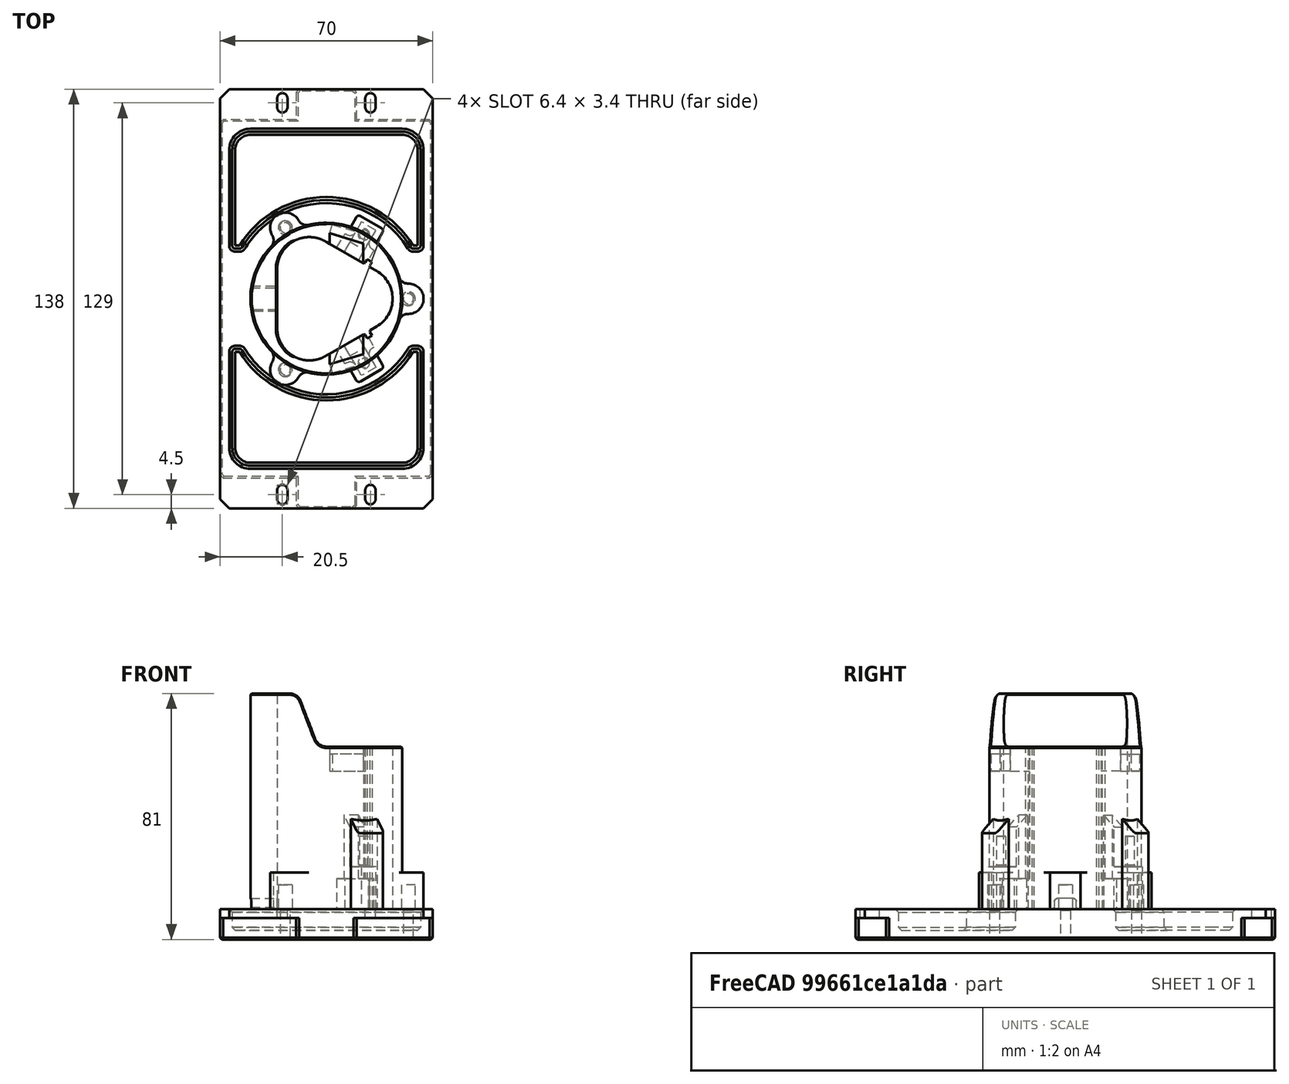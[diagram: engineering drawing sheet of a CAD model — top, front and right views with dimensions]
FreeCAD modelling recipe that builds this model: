
FCSTD DOCUMENT  (FreeCAD 1.2R20260204 (Git shallow))
Label: SupportBatterie
License: All rights reserved
LicenseURL: https://en.wikipedia.org/wiki/All_rights_reserved
objects: Sketcher::SketchObject×17, PartDesign::Pocket×12, PartDesign::Chamfer×11, PartDesign::Fillet×8, PartDesign::Pad×6, PartDesign::Mirrored×4, Image::ImagePlane×3, App::Point×3, PartDesign::Draft×2, PartDesign::Body×2, App::DocumentObjectGroup×1, PartDesign::PolarPattern×1, PartDesign::SubShapeBinder×1, App::Part×1
note: 164 computed .brp shape members not serialized (recipe doc carries the construction recipe); baked Part::Feature solids carry a one-line shape summary decoded from their .brp

FEATURE [Image::ImagePlane] IMG_20250729_205622
  Placement = pos=(4.02698,3.13465,0.3) rot=(0,0,1;0.021991rad)
  XSize = 54.8631
  YSize = 121.865
FEATURE [Image::ImagePlane] IMG_20250729_205825
  Placement = pos=(5.3,0,28.7) rot=(0.57735,0.57735,-0.57735;2.0944rad)
  XSize = 200.469
  YSize = 90.2503
FEATURE [Sketcher::SketchObject] Sketch
  ArcFitTolerance = 1e-06
  AttachmentSupport = -> [XY_Plane]
  ExternalTypes = [0]
  FullyConstrained = true
  MakeInternals = false
  MapMode = 5
  sketch-geometry (21):
    g0: ArcOfCircle CenterX=11.2267 CenterY=0 CenterZ=0 NormalX=0 NormalY=0 NormalZ=1 AngleXU=0 Radius=10.58 StartAngle=5.23599 EndAngle=7.33038
    g1: ArcOfCircle CenterX=-5.61333 CenterY=9.72258 CenterZ=0 NormalX=0 NormalY=0 NormalZ=1 AngleXU=0 Radius=10.58 StartAngle=1.0472 EndAngle=3.14159
    g2: ArcOfCircle CenterX=-5.61333 CenterY=-9.72258 CenterZ=0 NormalX=0 NormalY=0 NormalZ=1 AngleXU=0 Radius=10.58 StartAngle=3.14159 EndAngle=5.23599
    g3: LineSegment [constr] StartX=-0.323333 StartY=18.8851 StartZ=0 EndX=16.5167 EndY=9.16255 EndZ=0
    g4: LineSegment [constr] StartX=16.5167 StartY=-9.16255 StartZ=0 EndX=-0.323333 EndY=-18.8851 EndZ=0
    g5: LineSegment StartX=-16.1933 StartY=-9.72258 StartZ=0 EndX=-16.1933 EndY=9.72258 EndZ=0
    g6: LineSegment [constr] StartX=-5.61333 StartY=9.72258 StartZ=0 EndX=9e-16 EndY=0 EndZ=0
    g7: LineSegment [constr] StartX=0 StartY=0 StartZ=0 EndX=11.2267 EndY=0 EndZ=0
    g8: LineSegment [constr] StartX=0 StartY=0 StartZ=0 EndX=-5.61333 EndY=-9.72258 EndZ=0
    g9: GeomPoint [constr] X=21.8067 Y=0 Z=0
    g10: Circle CenterX=0 CenterY=0 CenterZ=0 NormalX=0 NormalY=0 NormalZ=1 AngleXU=0 Radius=25
    g11: LineSegment StartX=12.55 StartY=11.4527 StartZ=0 EndX=13.45 EndY=13.0116 EndZ=0
    g12: LineSegment StartX=13.45 StartY=13.0116 StartZ=0 EndX=15.0088 EndY=12.1116 EndZ=0
    g13: LineSegment StartX=15.0088 StartY=12.1116 StartZ=0 EndX=14.1088 EndY=10.5527 EndZ=0
    g14: LineSegment StartX=12.55 StartY=-11.4527 StartZ=0 EndX=13.45 EndY=-13.0116 EndZ=0
    g15: LineSegment StartX=13.45 StartY=-13.0116 StartZ=0 EndX=15.0088 EndY=-12.1116 EndZ=0
    g16: LineSegment StartX=15.0088 StartY=-12.1116 StartZ=0 EndX=14.1088 EndY=-10.5527 EndZ=0
    g17: LineSegment StartX=-0.323333 StartY=18.8851 StartZ=0 EndX=12.55 EndY=11.4527 EndZ=0
    g18: LineSegment StartX=14.1088 StartY=10.5527 StartZ=0 EndX=16.5167 EndY=9.16255 EndZ=0
    g19: LineSegment StartX=14.1088 StartY=-10.5527 StartZ=0 EndX=16.5167 EndY=-9.16255 EndZ=0
    g20: LineSegment StartX=12.55 StartY=-11.4527 StartZ=0 EndX=-0.323333 EndY=-18.8851 EndZ=0
  constraints (52):
    c: Equal(g1,g2)
    c: Equal(g2,g0)
    c: Vertical(g5)
    c: Tangent(g5,g1) = 1.5708
    c: Tangent(g3,g1) = 1.5708
    c: Tangent(g3,g0) = 1.5708
    c: Tangent(g4,g0) = 1.5708
    c: Tangent(g4,g2) = 1.5708
    c: Tangent(g5,g2) = 1.5708
    c: PointOnObject(g0,g-1)
    c: Equal(g5,g4)
    c: Equal(g4,g3)
    c: Coincident(g6,g1)
    c: Coincident(g6,g-1)
    c: Coincident(g7,g6)
    c: Coincident(g7,g0)
    c: Coincident(g8,g6)
    c: Coincident(g8,g2)
    c: Equal(g6,g7)
    c: PointOnObject(g9,g-1)
    c: PointOnObject(g9,g0)
    c: DistanceX(g1,g9) = 38
    c: Radius(g0) = 10.58
    c: Coincident(g10,g6)
    c: Diameter(g10) = 50
    c: PointOnObject(g11,g3)
    c: Coincident(g11,g12)
    c: Coincident(g12,g13)
    c: PointOnObject(g13,g3)
    c: Perpendicular(g12,g11)
    c: Perpendicular(g13,g12)
    c: Perpendicular(g3,g11)
    c: PointOnObject(g14,g4)
    c: Coincident(g14,g15)
    c: Coincident(g15,g16)
    c: Perpendicular(g15,g16)
    c: Perpendicular(g14,g15)
    c: Perpendicular(g4,g16)
    c: Equal(g15,g12)
    c: Symmetric(g13,g16,g-1)
    c: Equal(g13,g16)
    c: Distance(g12) = 1.8
    c: Distance(g11) = 1.8
    c: DistanceX(g10,g11) = 12.55
    c: Coincident(g17,g1)
    c: Coincident(g17,g11)
    c: Coincident(g18,g13)
    c: Coincident(g18,g0)
    c: Coincident(g19,g16)
    c: Coincident(g19,g0)
    c: Coincident(g20,g14)
    c: Coincident(g20,g2)
FEATURE [PartDesign::Pad] Pad
  AlongSketchNormal = false
  Direction = (0,0,1)
  Length = 61
  Length2 = 10
  Profile = -> Sketch
  ReferenceAxis = -> Sketch [N_Axis]
  Refine = true
  SideType = 0
  Suppressed = false
  Type = 0
  Type2 = 0
FEATURE [Sketcher::SketchObject] Sketch001
  ArcFitTolerance = 1e-06
  AttachmentSupport = -> [XY_Plane]
  ExternalGeometry = -> [Pad]
  ExternalTypes = [0]
  FullyConstrained = true
  MakeInternals = false
  MapMode = 5
  sketch-geometry (8):
    g0: LineSegment StartX=4.91 StartY=15.8637 StartZ=0 EndX=3.455 EndY=13.3435 EndZ=0
    g1: LineSegment StartX=3.455 StartY=13.3435 StartZ=0 EndX=9.99349 EndY=9.56853 EndZ=0
    g2: LineSegment StartX=9.99349 StartY=9.56853 StartZ=0 EndX=11.4485 EndY=12.0887 EndZ=0
    g3: LineSegment StartX=11.4485 StartY=12.0887 StartZ=0 EndX=4.91 EndY=15.8637 EndZ=0
    g4: LineSegment StartX=4.91 StartY=-15.8637 StartZ=0 EndX=3.455 EndY=-13.3435 EndZ=0
    g5: LineSegment StartX=3.455 StartY=-13.3435 StartZ=0 EndX=9.99349 EndY=-9.56853 EndZ=0
    g6: LineSegment StartX=9.99349 StartY=-9.56853 StartZ=0 EndX=11.4485 EndY=-12.0887 EndZ=0
    g7: LineSegment StartX=11.4485 StartY=-12.0887 StartZ=0 EndX=4.91 EndY=-15.8637 EndZ=0
  constraints (23):
    c: PointOnObject(g0,g-3)
    c: Coincident(g0,g1)
    c: Coincident(g1,g2)
    c: PointOnObject(g2,g-3)
    c: Coincident(g2,g3)
    c: Coincident(g3,g0)
    c: PointOnObject(g4,g-4)
    c: Coincident(g4,g5)
    c: Coincident(g5,g6)
    c: Coincident(g6,g7)
    c: Coincident(g7,g4)
    c: Equal(g7,g5)
    c: Equal(g5,g1)
    c: Equal(g1,g3)
    c: Equal(g2,g0)
    c: Equal(g0,g6)
    c: Equal(g6,g4)
    c: Perpendicular(g2,g1)
    c: Perpendicular(g6,g7)
    c: Symmetric(g6,g2,g-1)
    c: Distance(g3) = 7.55
    c: Distance(g2) = 2.91
    c: DistanceX(g-1,g0) = 4.91
FEATURE [PartDesign::Pad] Pad001
  AlongSketchNormal = false
  BaseFeature = -> Pad
  Direction = (0,0,1)
  Length = 1.5
  Length2 = 10
  Profile = -> Sketch001
  ReferenceAxis = -> Sketch001 [N_Axis]
  Refine = true
  SideType = 0
  Suppressed = false
  Type = 0
  Type2 = 0
FEATURE [PartDesign::Chamfer] Chamfer
  Angle = 45
  Base = -> Pad001 [Edge29,Edge35,Edge23,Edge18]
  BaseFeature = -> Pad001
  ChamferType = 0
  FlipDirection = false
  Refine = true
  Size = 0.4
  Size2 = 1
  SupportTransform = false
  Suppressed = false
  UseAllEdges = false
FEATURE [PartDesign::Fillet] Fillet
  Base = -> Chamfer [Edge81,Edge77,Edge72,Edge76]
  BaseFeature = -> Chamfer
  Radius = 0.6
  Refine = true
  SupportTransform = false
  Suppressed = false
  UseAllEdges = false
FEATURE [PartDesign::Chamfer] Chamfer001
  Angle = 45
  Base = -> Fillet [Face32]
  BaseFeature = -> Fillet
  ChamferType = 0
  FlipDirection = false
  Refine = true
  Size = 0.4
  Size2 = 1
  SupportTransform = false
  Suppressed = false
  UseAllEdges = false
FEATURE [Sketcher::SketchObject] Sketch002
  ArcFitTolerance = 1e-06
  AttachmentSupport = -> [XZ_Plane]
  ExternalGeometry = -> [Chamfer001]
  ExternalTypes = [0]
  FullyConstrained = true
  MakeInternals = false
  MapMode = 5
  Placement = pos=(0,0,0) rot=(1,0,0;1.5708rad)
  sketch-geometry (4):
    g0: LineSegment StartX=-9.41 StartY=61 StartZ=0 EndX=-2.71 EndY=43.5 EndZ=0
    g1: LineSegment StartX=-2.71 StartY=43.5 StartZ=0 EndX=25 EndY=43.5 EndZ=0
    g2: LineSegment StartX=25 StartY=43.5 StartZ=0 EndX=25 EndY=61 EndZ=0
    g3: LineSegment StartX=-9.41 StartY=61 StartZ=0 EndX=25 EndY=61 EndZ=0
  constraints (12):
    c: Coincident(g1,g0)
    c: Coincident(g2,g1)
    c: Vertical(g2)
    c: Coincident(g3,g0)
    c: Coincident(g3,g2)
    c: Horizontal(g3)
    c: Horizontal(g1)
    c: DistanceY(g2,g2) = 17.5
    c: PointOnObject(g-3,g3)
    c: PointOnObject(g-4,g2)
    c: DistanceX(g3,g3) = 34.41
    c: DistanceX(g1,g1) = 27.71
FEATURE [PartDesign::Pocket] Pocket
  AlongSketchNormal = false
  BaseFeature = -> Chamfer001
  Direction = (0,1,-2e-16)
  Length = 60
  Length2 = 10
  Profile = -> Sketch002
  ReferenceAxis = -> Sketch002 [N_Axis]
  Refine = true
  SideType = 2
  Suppressed = false
  Type = 0
  Type2 = 0
FEATURE [PartDesign::Fillet] Fillet001
  Base = -> Pocket [Edge106,Edge67,Edge51,Edge111]
  BaseFeature = -> Pocket
  Radius = 4
  Refine = true
  SupportTransform = false
  Suppressed = false
  UseAllEdges = false
FEATURE [Image::ImagePlane] IMG_20250729_205826  label="IMG_20250729_205826_205826"
  Placement = pos=(4.02698,3.13465,43.6) rot=(0,0,1;0.021991rad)
  XSize = 54.8631
  YSize = 121.865
FEATURE [Sketcher::SketchObject] Sketch003
  ArcFitTolerance = 1e-06
  AttachmentSupport = -> [Fillet001]
  ExternalGeometry = -> [Fillet001]
  ExternalTypes = [0]
  FullyConstrained = true
  MakeInternals = false
  MapMode = 5
  Placement = pos=(0,9.7e-15,43.5) rot=(0,0,1;0rad)
  sketch-geometry (4):
    g0: LineSegment StartX=1.07 StartY=18.0807 StartZ=0 EndX=1.07 EndY=21.5807 EndZ=0
    g1: LineSegment StartX=12.07 StartY=18.2298 StartZ=0 EndX=12.07 EndY=11.7298 EndZ=0
    g2: LineSegment StartX=1.07 StartY=18.0807 StartZ=0 EndX=12.07 EndY=11.7298 EndZ=0
    g3: LineSegment StartX=1.07 StartY=21.5807 StartZ=0 EndX=12.07 EndY=18.2298 EndZ=0
  constraints (12):
    c: Vertical(g0)
    c: Vertical(g1)
    c: Coincident(g2,g0)
    c: Coincident(g2,g1)
    c: DistanceX(g0) = 1.07
    c: DistanceY(g0,g0) = 3.5
    c: DistanceY(g1,g1) = 6.5
    c: DistanceX(g0,g1) = 11
    c: Coincident(g3,g0)
    c: Coincident(g3,g1)
    c: PointOnObject(g0,g-3)
    c: PointOnObject(g1,g-3)
FEATURE [PartDesign::Pocket] Pocket001
  AlongSketchNormal = false
  BaseFeature = -> Fillet001
  Direction = (0,0,-1)
  Length = 8
  Length2 = 10
  Profile = -> Sketch003
  ReferenceAxis = -> Sketch003 [N_Axis]
  Refine = true
  SideType = 0
  Suppressed = false
  Type = 0
  Type2 = 0
FEATURE [Sketcher::SketchObject] Sketch004
  ArcFitTolerance = 1e-06
  AttachmentSupport = -> [Pocket001]
  ExternalGeometry = -> [Pocket001]
  ExternalTypes = [0]
  FullyConstrained = true
  MakeInternals = false
  MapMode = 5
  Placement = pos=(6.1066,20.0464,0) rot=(0.978531,-0.145736,-0.145736;1.5925rad)
  sketch-geometry (4):
    g0: LineSegment StartX=-5.2651 StartY=35.5 StartZ=0 EndX=6.23395 EndY=35.5 EndZ=0
    g1: LineSegment StartX=6.23395 StartY=35.5 StartZ=0 EndX=6.23395 EndY=41 EndZ=0
    g2: LineSegment StartX=6.23395 StartY=41 StartZ=0 EndX=-5.2651 EndY=41 EndZ=0
    g3: LineSegment StartX=-5.2651 StartY=41 StartZ=0 EndX=-5.2651 EndY=35.5 EndZ=0
  constraints (11):
    c: Coincident(g0,g1)
    c: Coincident(g1,g2)
    c: Coincident(g2,g3)
    c: Coincident(g3,g0)
    c: Horizontal(g2)
    c: Vertical(g1)
    c: Vertical(g3)
    c: Coincident(g0,g-3)
    c: Coincident(g0,g-3)
    c: DistanceY(g1,g1) = 5.5
    c: DistanceY(g1,g-4) = 2.5
FEATURE [PartDesign::Pocket] Pocket002
  AlongSketchNormal = false
  BaseFeature = -> Pocket001
  Direction = (0.291403,0.956601,1e-16)
  Length = 3
  Length2 = 10
  Profile = -> Sketch004
  ReferenceAxis = -> Sketch004 [N_Axis]
  Refine = true
  SideType = 0
  Suppressed = false
  Type = 0
  Type2 = 0
FEATURE [PartDesign::Mirrored] Mirrored
  BaseFeature = -> Pocket002
  MirrorPlane = -> XZ_Plane
  Originals = -> [Pocket001,Pocket002]
  Refine = true
  Suppressed = false
  TransformMode = 0
FEATURE [PartDesign::Chamfer] Chamfer002
  Angle = 45
  Base = -> Mirrored [Edge19]
  BaseFeature = -> Mirrored
  ChamferType = 0
  FlipDirection = false
  Refine = true
  Size = 0.4
  Size2 = 1
  SupportTransform = false
  Suppressed = false
  UseAllEdges = false
FEATURE [App::DocumentObjectGroup] Group  label="Images"
  Group = -> [IMG_20250729_205622,IMG_20250729_205825,IMG_20250729_205826]
FEATURE [App::Point] Origin001  label="Origine"
  Role = Origin
FEATURE [Sketcher::SketchObject] Sketch005
  ArcFitTolerance = 1e-06
  AttachmentSupport = -> [Chamfer002]
  ExternalGeometry = -> [Chamfer002]
  ExternalTypes = [0,0,0]
  FullyConstrained = true
  MakeInternals = false
  MapMode = 5
  Placement = pos=(0,0,0) rot=(1,0,0;3.14159rad)
  sketch-geometry (13):
    g0: LineSegment [constr] StartX=4.91 StartY=15.8637 StartZ=0 EndX=11.4485 EndY=12.0887 EndZ=0
    g1: LineSegment [constr] StartX=7.79768 StartY=18.8153 StartZ=0 EndX=4.34268 EndY=12.831 EndZ=0
    g2: LineSegment [constr] StartX=4.34268 StartY=12.831 StartZ=0 EndX=9.10582 EndY=10.081 EndZ=0
    g3: LineSegment [constr] StartX=9.10582 StartY=10.081 StartZ=0 EndX=12.5608 EndY=16.0653 EndZ=0
    g4: LineSegment StartX=12.5608 StartY=16.0653 StartZ=0 EndX=7.79768 EndY=18.8153 EndZ=0
    g5: GeomPoint X=6.72425 Y=11.456 Z=0
    g6: LineSegment StartX=7.79768 StartY=18.8153 StartZ=0 EndX=5.79768 EndY=15.3512 EndZ=0
    g7: LineSegment StartX=4.91 StartY=15.8637 StartZ=0 EndX=3.45499 EndY=13.3435 EndZ=0
    g8: LineSegment StartX=3.45499 StartY=13.3435 StartZ=0 EndX=9.99349 EndY=9.56853 EndZ=0
    g9: LineSegment StartX=9.99349 StartY=9.56853 StartZ=0 EndX=11.4485 EndY=12.0887 EndZ=0
    g10: LineSegment StartX=11.4485 StartY=12.0887 StartZ=0 EndX=10.5608 EndY=12.6012 EndZ=0
    g11: LineSegment StartX=10.5608 StartY=12.6012 StartZ=0 EndX=12.5608 EndY=16.0653 EndZ=0
    g12: LineSegment StartX=4.91 StartY=15.8637 StartZ=0 EndX=5.79768 EndY=15.3512 EndZ=0
  constraints (32):
    c: Coincident(g0,g-3)
    c: Coincident(g0,g-4)
    c: Coincident(g1,g2)
    c: Coincident(g2,g3)
    c: Coincident(g3,g4)
    c: Coincident(g4,g1)
    c: Parallel(g1,g3)
    c: Parallel(g2,g4)
    c: Perpendicular(g1,g2)
    c: PointOnObject(g1,g-5)
    c: Distance(g0,g4) = 4
    c: Symmetric(g2,g2,g5)
    c: Symmetric(g-5,g-5,g5)
    c: Coincident(g6,g1)
    c: PointOnObject(g6,g1)
    c: Coincident(g7,g0)
    c: Coincident(g8,g7)
    c: Coincident(g9,g8)
    c: Coincident(g9,g0)
    c: Coincident(g10,g0)
    c: PointOnObject(g10,g3)
    c: Coincident(g11,g10)
    c: Coincident(g11,g3)
    c: Distance(g4,g4) = 5.5
    c: PointOnObject(g10,g0)
    c: PointOnObject(g6,g0)
    c: Coincident(g12,g0)
    c: Coincident(g12,g6)
    c: PointOnObject(g-5,g8)
    c: PointOnObject(g-5,g8)
    c: Equal(g7,g9)
    c: Perpendicular(g10,g9)
FEATURE [PartDesign::Pocket] Pocket003
  BaseFeature = -> Chamfer002
  Direction = (0,0,1)
  Length = 17
  Length2 = 5
  Profile = -> Sketch005
  ReferenceAxis = -> Sketch005 [N_Axis]
  Refine = true
  SideType = 0
  Suppressed = false
  Type = 0
  Type2 = 0
FEATURE [PartDesign::Draft] Draft
  Angle = -45
  Base = -> Pocket003 [Face55]
  BaseFeature = -> Pocket003
  NeutralPlane = -> Pocket003 [Face56]
  Refine = true
  SupportTransform = false
  Suppressed = false
FEATURE [Sketcher::SketchObject] Sketch006
  ArcFitTolerance = 1e-06
  AttachmentSupport = -> [Draft]
  ExternalGeometry = -> [Draft]
  ExternalTypes = [0]
  FullyConstrained = true
  MakeInternals = false
  MapMode = 5
  Placement = pos=(0,0,0) rot=(1,0,0;3.14159rad)
  sketch-geometry (5):
    g0: LineSegment StartX=5.84912 StartY=19.9403 StartZ=0 EndX=14.5094 EndY=14.9403 EndZ=0
    g1: LineSegment StartX=14.5094 StartY=14.9403 StartZ=0 EndX=19.0094 EndY=22.7345 EndZ=0
    g2: LineSegment StartX=19.0094 StartY=22.7345 StartZ=0 EndX=10.3491 EndY=27.7345 EndZ=0
    g3: LineSegment StartX=10.3491 StartY=27.7345 StartZ=0 EndX=5.84912 EndY=19.9403 EndZ=0
    g4: GeomPoint X=10.1792 Y=17.4403 Z=0
  constraints (12):
    c: Coincident(g0,g1)
    c: Coincident(g1,g2)
    c: Coincident(g2,g3)
    c: Coincident(g3,g0)
    c: Parallel(g0,g2)
    c: Parallel(g1,g3)
    c: PointOnObject(g0,g-3)
    c: Perpendicular(g1,g0)
    c: Symmetric(g0,g0,g4)
    c: Symmetric(g-3,g-3,g4)
    c: Distance(g2,g2) = 10
    c: Distance(g1,g1) = 9
FEATURE [PartDesign::Pad] Pad002
  BaseFeature = -> Draft
  Direction = (0,0,-1)
  Length = 15
  Length2 = 10
  Profile = -> Sketch006
  ReferenceAxis = -> Sketch006 [N_Axis]
  Refine = true
  Reversed = true
  SideType = 0
  Suppressed = false
  Type = 0
  Type2 = 0
FEATURE [PartDesign::Draft] Draft001
  Angle = 45
  Base = -> Pad002 [Face57]
  BaseFeature = -> Pad002
  NeutralPlane = -> Pad002 [Face68]
  Refine = true
  SupportTransform = false
  Suppressed = false
FEATURE [PartDesign::Fillet] Fillet002
  Base = -> Draft001 [Edge178,Edge182]
  BaseFeature = -> Draft001
  Radius = 1
  Refine = true
  SupportTransform = false
  Suppressed = false
  UseAllEdges = false
FEATURE [Sketcher::SketchObject] Sketch007
  ArcFitTolerance = 1e-06
  AttachmentSupport = -> [Fillet002]
  ExternalGeometry = -> [Fillet002]
  ExternalTypes = [0]
  FullyConstrained = true
  MakeInternals = false
  MapMode = 5
  Placement = pos=(0,0,0) rot=(1,0,0;3.14159rad)
  sketch-geometry (4):
    g0: LineSegment StartX=7.79768 StartY=18.8153 StartZ=0 EndX=12.5608 EndY=16.0653 EndZ=0
    g1: LineSegment StartX=12.5608 StartY=16.0653 StartZ=0 EndX=16.3108 EndY=22.5605 EndZ=0
    g2: LineSegment StartX=16.3108 StartY=22.5605 StartZ=0 EndX=11.5477 EndY=25.3105 EndZ=0
    g3: LineSegment StartX=11.5477 StartY=25.3105 StartZ=0 EndX=7.79768 EndY=18.8153 EndZ=0
  constraints (10):
    c: Coincident(g0,g1)
    c: Coincident(g1,g2)
    c: Coincident(g2,g3)
    c: Coincident(g3,g0)
    c: Parallel(g0,g2)
    c: Parallel(g1,g3)
    c: Perpendicular(g1,g0)
    c: Coincident(g0,g-3)
    c: Coincident(g0,g-3)
    c: Distance(g1,g1) = 7.5
FEATURE [PartDesign::Pocket] Pocket004
  BaseFeature = -> Fillet002
  Direction = (0,0,1)
  Length = 4
  Length2 = 5
  Profile = -> Sketch007
  ReferenceAxis = -> Sketch007 [N_Axis]
  Refine = true
  SideType = 0
  Suppressed = false
  Type = 0
  Type2 = 0
FEATURE [Sketcher::SketchObject] Sketch008
  ArcFitTolerance = 1e-06
  AttachmentSupport = -> [Pocket004]
  ExternalGeometry = -> [Pocket004]
  ExternalTypes = [0]
  FullyConstrained = true
  MakeInternals = false
  MapMode = 5
  Placement = pos=(0,0,4) rot=(1,0,0;3.14159rad)
  sketch-geometry (2):
    g0: Circle CenterX=12.3292 CenterY=21.1642 CenterZ=0 NormalX=0 NormalY=0 NormalZ=1 AngleXU=0 Radius=1.5
    g1: LineSegment [constr] StartX=10.1792 StartY=17.4403 StartZ=0 EndX=13.9292 EndY=23.9355 EndZ=0
  constraints (5):
    c: Diameter(g0) = 3
    c: Symmetric(g-3,g-3,g1)
    c: Symmetric(g-5,g-5,g1)
    c: PointOnObject(g0,g1)
    c: Distance(g0,g-3) = 4.3
FEATURE [PartDesign::Pocket] Pocket005
  BaseFeature = -> Pocket004
  Direction = (0,0,1)
  Length = 10
  Length2 = 5
  Profile = -> Sketch008
  ReferenceAxis = -> Sketch008 [N_Axis]
  Refine = true
  SideType = 0
  Suppressed = false
  Type = 0
  Type2 = 0
FEATURE [PartDesign::Chamfer] Chamfer003
  Angle = 45
  Base = -> Pocket005 [Edge156]
  BaseFeature = -> Pocket005
  ChamferType = 0
  FlipDirection = false
  Refine = true
  Size = 0.4
  Size2 = 1
  SupportTransform = false
  Suppressed = false
  UseAllEdges = false
FEATURE [PartDesign::Mirrored] Mirrored001
  BaseFeature = -> Chamfer003
  MirrorPlane = -> XZ_Plane
  Originals = -> [Pocket003,Draft,Pad002,Draft001,Fillet002,Pocket004,Pocket005,Chamfer003]
  Refine = true
  Suppressed = false
  TransformMode = 0
FEATURE [PartDesign::Pad] Pad003
  BaseFeature = -> Mirrored001
  Direction = (0,0,-1)
  Length = 10
  Length2 = 10
  Profile = -> Mirrored001 [Face76]
  Refine = true
  SideType = 0
  Suppressed = false
  Type = 0
  Type2 = 0
FEATURE [Sketcher::SketchObject] Sketch009
  ArcFitTolerance = 1e-06
  AttachmentSupport = -> [Pad003]
  ExternalGeometry = -> [Pad003]
  ExternalTypes = [0,0,0,0,0,0]
  FullyConstrained = true
  MakeInternals = false
  MapMode = 5
  Placement = pos=(0,0,-10) rot=(1,0,0;3.14159rad)
  sketch-geometry (7):
    g0: ArcOfCircle [constr] CenterX=0 CenterY=0 CenterZ=0 NormalX=0 NormalY=0 NormalZ=1 AngleXU=0 Radius=5 StartAngle=1.5708 EndAngle=4.71239
    g1: ArcOfCircle CenterX=27 CenterY=0 CenterZ=0 NormalX=0 NormalY=0 NormalZ=1 AngleXU=0 Radius=5 StartAngle=4.71239 EndAngle=7.85398
    g2: LineSegment [constr] StartX=-8e-16 StartY=5 StartZ=0 EndX=27 EndY=5 EndZ=0
    g3: LineSegment [constr] StartX=-9e-16 StartY=-5 StartZ=0 EndX=27 EndY=-5 EndZ=0
    g4: ArcOfCircle CenterX=0 CenterY=0 CenterZ=0 NormalX=0 NormalY=0 NormalZ=1 AngleXU=0 Radius=25 StartAngle=6.08183 EndAngle=6.48454
    g5: LineSegment StartX=24.4949 StartY=5 StartZ=0 EndX=27 EndY=5 EndZ=0
    g6: LineSegment StartX=27 StartY=-5 StartZ=0 EndX=24.4949 EndY=-5 EndZ=0
  constraints (17):
    c: Tangent(g0,g2) = 1.5708
    c: Tangent(g0,g3) = -1.5708
    c: Tangent(g1,g2) = 1.5708
    c: Tangent(g1,g3) = -1.5708
    c: Equal(g0,g1)
    c: Coincident(g0,g-5)
    c: DistanceX(g-5,g1) = 2
    c: Distance(g1,g1) = 10
    c: PointOnObject(g1,g-1)
    c: Coincident(g4,g0)
    c: PointOnObject(g4,g-4)
    c: PointOnObject(g4,g3)
    c: PointOnObject(g4,g2)
    c: Coincident(g5,g4)
    c: Coincident(g5,g1)
    c: Coincident(g6,g1)
    c: Coincident(g6,g4)
FEATURE [PartDesign::Pad] Pad004
  BaseFeature = -> Pad003
  Direction = (0,0,-1)
  Length = 12
  Length2 = 10
  Profile = -> Sketch009
  ReferenceAxis = -> Sketch009 [N_Axis]
  Refine = true
  Reversed = true
  SideType = 0
  Suppressed = false
  Type = 0
  Type2 = 0
FEATURE [PartDesign::Fillet] Fillet003
  Base = -> Pad004 [Edge126,Edge116]
  BaseFeature = -> Pad004
  Radius = 3
  Refine = true
  SupportTransform = false
  Suppressed = false
  UseAllEdges = false
FEATURE [Sketcher::SketchObject] Sketch010
  ArcFitTolerance = 1e-06
  AttachmentSupport = -> [Fillet003]
  ExternalGeometry = -> [Fillet003]
  ExternalTypes = [0]
  FullyConstrained = true
  MakeInternals = false
  MapMode = 5
  Placement = pos=(0,0,-10) rot=(1,0,0;3.14159rad)
  sketch-geometry (1):
    g0: Circle CenterX=27 CenterY=0 CenterZ=0 NormalX=0 NormalY=0 NormalZ=1 AngleXU=0 Radius=2.3
  constraints (2):
    c: Coincident(g0,g-3)
    c: Diameter(g0) = 4.6
FEATURE [PartDesign::Pocket] Pocket006
  BaseFeature = -> Fillet003
  Direction = (0,0,1)
  Length = 8
  Length2 = 5
  Profile = -> Sketch010
  ReferenceAxis = -> Sketch010 [N_Axis]
  Refine = true
  SideType = 0
  Suppressed = false
  Type = 0
  Type2 = 0
FEATURE [PartDesign::PolarPattern] PolarPattern
  Angle = 360
  Axis = -> Z_Axis
  BaseFeature = -> Pocket006
  Mode = 0
  Occurrences = 3
  Offset = 120
  Originals = -> [Pad004,Fillet003,Pocket006]
  Refine = true
  SpacingPattern = [0]
  Spacings = [-1,-1]
  Suppressed = false
  TransformMode = 0
FEATURE [Sketcher::SketchObject] Sketch011
  ArcFitTolerance = 1e-06
  AttachmentSupport = -> [PolarPattern]
  ExternalGeometry = -> [PolarPattern]
  ExternalTypes = [0]
  FullyConstrained = true
  MakeInternals = false
  MapMode = 5
  Placement = pos=(0,0,-10) rot=(1,0,0;3.14159rad)
  sketch-geometry (5):
    g0: LineSegment StartX=-25 StartY=-3.6 StartZ=0 EndX=0 EndY=-3.6 EndZ=0
    g1: LineSegment StartX=0 StartY=-3.6 StartZ=0 EndX=0 EndY=3.6 EndZ=0
    g2: LineSegment StartX=0 StartY=3.6 StartZ=0 EndX=-25 EndY=3.6 EndZ=0
    g3: LineSegment StartX=-25 StartY=3.6 StartZ=0 EndX=-25 EndY=-3.6 EndZ=0
    g4: GeomPoint [constr] X=-12.5 Y=0 Z=0
  constraints (13):
    c: Coincident(g0,g1)
    c: Coincident(g1,g2)
    c: Coincident(g2,g3)
    c: Coincident(g3,g0)
    c: Horizontal(g0)
    c: Horizontal(g2)
    c: Vertical(g1)
    c: Vertical(g3)
    c: Symmetric(g2,g0,g4)
    c: PointOnObject(g4,g-1)
    c: PointOnObject(g1,g-2)
    c: Tangent(g3,g-3)
    c: DistanceY(g3,g3) = 7.2
FEATURE [PartDesign::Pocket] Pocket007
  BaseFeature = -> PolarPattern
  Direction = (0,0,1)
  Length = 3.5
  Length2 = 5
  Profile = -> Sketch011
  ReferenceAxis = -> Sketch011 [N_Axis]
  Refine = true
  SideType = 0
  Suppressed = false
  Type = 0
  Type2 = 0
FEATURE [PartDesign::Fillet] Fillet004
  Base = -> Pocket007 [Edge147,Edge145]
  BaseFeature = -> Pocket007
  Radius = 1
  Refine = true
  SupportTransform = false
  Suppressed = false
  UseAllEdges = false
FEATURE [PartDesign::Chamfer] Chamfer004
  Angle = 45
  Base = -> Fillet004 [Edge60,Edge46]
  BaseFeature = -> Fillet004
  ChamferType = 0
  FlipDirection = false
  Refine = true
  Size = 0.6
  Size2 = 1
  SupportTransform = false
  Suppressed = false
  UseAllEdges = false
FEATURE [Sketcher::SketchObject] Sketch012
  ArcFitTolerance = 1e-06
  AttachmentSupport = -> [Chamfer004]
  ExternalGeometry = -> [Chamfer004]
  ExternalTypes = [0,0,0,0,0,0]
  FullyConstrained = true
  MakeInternals = false
  MapMode = 5
  Placement = pos=(0,0,-10) rot=(1,0,0;3.14159rad)
  sketch-geometry (10):
    g0: LineSegment StartX=15.6924 StartY=15.9893 StartZ=0 EndX=6.16611 EndY=21.4893 EndZ=0
    g1: LineSegment StartX=6.16611 StartY=21.4893 StartZ=0 EndX=0.666106 EndY=11.963 EndZ=0
    g2: LineSegment StartX=0.666106 StartY=11.963 StartZ=0 EndX=10.1924 EndY=6.46302 EndZ=0
    g3: LineSegment StartX=10.1924 StartY=6.46302 StartZ=0 EndX=15.6924 EndY=15.9893 EndZ=0
    g4: Circle [constr] CenterX=8.17925 CenterY=13.9762 CenterZ=0 NormalX=0 NormalY=0 NormalZ=1 AngleXU=0 Radius=7.77817
    g5: LineSegment StartX=10.1924 StartY=-6.46302 StartZ=0 EndX=0.666106 EndY=-11.963 EndZ=0
    g6: LineSegment StartX=0.666106 StartY=-11.963 StartZ=0 EndX=6.16611 EndY=-21.4893 EndZ=0
    g7: LineSegment StartX=6.16611 StartY=-21.4893 StartZ=0 EndX=15.6924 EndY=-15.9893 EndZ=0
    g8: LineSegment StartX=15.6924 StartY=-15.9893 StartZ=0 EndX=10.1924 EndY=-6.46302 EndZ=0
    g9: Circle [constr] CenterX=8.17925 CenterY=-13.9762 CenterZ=0 NormalX=0 NormalY=0 NormalZ=1 AngleXU=0 Radius=7.77817
  constraints (28):
    c: Coincident(g0,g1)
    c: Coincident(g1,g2)
    c: Coincident(g2,g3)
    c: Coincident(g3,g0)
    c: Equal(g0,g1)
    c: Equal(g0,g2)
    c: Equal(g0,g3)
    c: PointOnObject(g0,g4)
    c: PointOnObject(g1,g4)
    c: PointOnObject(g2,g4)
    c: PointOnObject(g3,g4)
    c: Symmetric(g-7,g-7,g4)
    c: Coincident(g5,g6)
    c: Coincident(g6,g7)
    c: Coincident(g7,g8)
    c: Coincident(g8,g5)
    c: Equal(g5,g6)
    c: Equal(g5,g7)
    c: Equal(g5,g8)
    c: PointOnObject(g5,g9)
    c: PointOnObject(g6,g9)
    c: PointOnObject(g7,g9)
    c: PointOnObject(g8,g9)
    c: Symmetric(g-8,g-8,g9)
    c: Parallel(g5,g-8)
    c: Parallel(g2,g-7)
    c: Equal(g2,g5)
    c: Distance(g2,g2) = 11
FEATURE [PartDesign::Pocket] Pocket008
  BaseFeature = -> Chamfer004
  Direction = (0,0,1)
  Length = 10
  Length2 = 5
  Profile = -> Sketch012
  ReferenceAxis = -> Sketch012 [N_Axis]
  Refine = true
  SideType = 0
  Suppressed = false
  Type = 0
  Type2 = 0
FEATURE [PartDesign::Fillet] Fillet005
  Base = -> Pocket008 [Edge243,Edge258,Edge211,Edge201]
  BaseFeature = -> Pocket008
  Radius = 2
  Refine = true
  SupportTransform = false
  Suppressed = false
  UseAllEdges = false
FEATURE [PartDesign::Body] Body  label="battery-support"
  AllowCompound = true
  Group = -> [Sketch,Pad,Sketch001,Pad001,Chamfer,Fillet,Chamfer001,Sketch002,Pocket,Fillet001,Sketch003,Pocket001,Sketch004,Pocket002,Mirrored,Chamfer002,Sketch005,Pocket003,Draft,Sketch006,Pad002,Draft001,Fillet002,Sketch007,Pocket004,Sketch008,Pocket005,Chamfer003,Mirrored001,Pad003,Sketch009,Pad004,Fillet003,Sketch010,Pocket006,PolarPattern,Sketch011,Pocket007,Fillet004,Chamfer004,Sketch012,Pocket008,+1 more]
  Origin = -> Origin
  Tip = -> Fillet005
FEATURE [App::Point] Origin003  label="Origine001"
  Role = Origin
FEATURE [PartDesign::SubShapeBinder] Binder
  BindCopyOnChange = 0
  BindMode = 0
  ClaimChildren = false
  Context = -> Body001 [Binder.]
  Fuse = false
  MakeFace = true
  OffsetFill = false
  OffsetIntersection = false
  OffsetJoinType = 0
  OffsetOpenResult = false
  PartialLoad = false
  Refine = true
  Relative = true
  Support = -> [Body[Fillet005.Face1]]
  _Version = 2
FEATURE [Sketcher::SketchObject] Sketch013
  ArcFitTolerance = 1e-06
  AttachmentSupport = -> [Origin002]
  ExternalGeometry = -> [Binder]
  ExternalTypes = [0,0,0]
  FullyConstrained = true
  MakeInternals = false
  MapMode = 5
  sketch-geometry (8):
    g0: LineSegment StartX=-35 StartY=-69 StartZ=0 EndX=35 EndY=-69 EndZ=0
    g1: LineSegment StartX=35 StartY=-69 StartZ=0 EndX=35 EndY=69 EndZ=0
    g2: LineSegment StartX=35 StartY=69 StartZ=0 EndX=-35 EndY=69 EndZ=0
    g3: LineSegment StartX=-35 StartY=69 StartZ=0 EndX=-35 EndY=-69 EndZ=0
    g4: GeomPoint [constr] X=0 Y=0 Z=0
    g5: Circle CenterX=-13.5 CenterY=23.3827 CenterZ=0 NormalX=0 NormalY=0 NormalZ=1 AngleXU=0 Radius=1.65
    g6: Circle CenterX=27 CenterY=0 CenterZ=0 NormalX=0 NormalY=0 NormalZ=1 AngleXU=0 Radius=1.65
    g7: Circle CenterX=-13.5 CenterY=-23.3827 CenterZ=0 NormalX=0 NormalY=0 NormalZ=1 AngleXU=0 Radius=1.65
  constraints (18):
    c: Coincident(g0,g1)
    c: Coincident(g1,g2)
    c: Coincident(g2,g3)
    c: Coincident(g3,g0)
    c: Horizontal(g0)
    c: Horizontal(g2)
    c: Vertical(g1)
    c: Vertical(g3)
    c: Symmetric(g2,g0,g4)
    c: Coincident(g4,g-1)
    c: DistanceY(g3,g3) = 138
    c: DistanceX(g2,g2) = 70
    c: Coincident(g5,g-3)
    c: Coincident(g6,g-4)
    c: Coincident(g7,g-5)
    c: Equal(g7,g6)
    c: Equal(g6,g5)
    c: Diameter(g6) = 3.3
FEATURE [PartDesign::Pad] Pad005
  Direction = (0,0,1)
  Length = 10
  Length2 = 10
  Profile = -> Sketch013
  ReferenceAxis = -> Sketch013 [N_Axis]
  Refine = true
  SideType = 0
  Suppressed = false
  Type = 0
  Type2 = 0
FEATURE [Sketcher::SketchObject] Sketch014
  ArcFitTolerance = 1e-06
  AttachmentSupport = -> [Pad005]
  ExternalGeometry = -> [Pad005]
  ExternalTypes = [0,0,0,0]
  FullyConstrained = true
  MakeInternals = false
  MapMode = 5
  Placement = pos=(0,0,0) rot=(1,0,0;3.14159rad)
  sketch-geometry (16):
    g0: LineSegment StartX=-35 StartY=69 StartZ=0 EndX=-35 EndY=59 EndZ=0
    g1: LineSegment StartX=-35 StartY=59 StartZ=0 EndX=-10 EndY=59 EndZ=0
    g2: LineSegment StartX=-10 StartY=59 StartZ=0 EndX=-10 EndY=69 EndZ=0
    g3: LineSegment StartX=-10 StartY=69 StartZ=0 EndX=-35 EndY=69 EndZ=0
    g4: LineSegment StartX=35 StartY=69 StartZ=0 EndX=10 EndY=69 EndZ=0
    g5: LineSegment StartX=10 StartY=69 StartZ=0 EndX=10 EndY=59 EndZ=0
    g6: LineSegment StartX=10 StartY=59 StartZ=0 EndX=35 EndY=59 EndZ=0
    g7: LineSegment StartX=35 StartY=59 StartZ=0 EndX=35 EndY=69 EndZ=0
    g8: LineSegment StartX=-35 StartY=-69 StartZ=0 EndX=-10 EndY=-69 EndZ=0
    g9: LineSegment StartX=-10 StartY=-69 StartZ=0 EndX=-10 EndY=-59 EndZ=0
    g10: LineSegment StartX=-10 StartY=-59 StartZ=0 EndX=-35 EndY=-59 EndZ=0
    g11: LineSegment StartX=-35 StartY=-59 StartZ=0 EndX=-35 EndY=-69 EndZ=0
    g12: LineSegment StartX=35 StartY=-69 StartZ=0 EndX=35 EndY=-59 EndZ=0
    g13: LineSegment StartX=35 StartY=-59 StartZ=0 EndX=10 EndY=-59 EndZ=0
    g14: LineSegment StartX=10 StartY=-59 StartZ=0 EndX=10 EndY=-69 EndZ=0
    g15: LineSegment StartX=10 StartY=-69 StartZ=0 EndX=35 EndY=-69 EndZ=0
  constraints (44):
    c: Coincident(g0,g1)
    c: Coincident(g1,g2)
    c: Coincident(g2,g3)
    c: Coincident(g3,g0)
    c: Vertical(g0)
    c: Vertical(g2)
    c: Horizontal(g1)
    c: Horizontal(g3)
    c: Coincident(g0,g-4)
    c: Coincident(g4,g5)
    c: Coincident(g5,g6)
    c: Coincident(g6,g7)
    c: Coincident(g7,g4)
    c: Horizontal(g4)
    c: Horizontal(g6)
    c: Vertical(g5)
    c: Vertical(g7)
    c: Coincident(g4,g-5)
    c: Coincident(g8,g9)
    c: Coincident(g9,g10)
    c: Coincident(g10,g11)
    c: Coincident(g11,g8)
    c: Horizontal(g8)
    c: Horizontal(g10)
    c: Vertical(g9)
    c: Vertical(g11)
    c: Coincident(g8,g-6)
    c: Coincident(g12,g13)
    c: Coincident(g13,g14)
    c: Coincident(g14,g15)
    c: Coincident(g15,g12)
    c: Vertical(g12)
    c: Vertical(g14)
    c: Horizontal(g13)
    c: Horizontal(g15)
    c: Coincident(g12,g-6)
    c: Equal(g14,g9)
    c: Equal(g9,g2)
    c: Equal(g2,g5)
    c: Equal(g6,g1)
    c: Equal(g1,g10)
    c: Equal(g10,g13)
    c: Distance(g6,g6) = 25
    c: Distance(g7,g7) = 10
FEATURE [PartDesign::Pocket] Pocket009
  BaseFeature = -> Pad005
  Direction = (0,0,1)
  Length = 7
  Length2 = 5
  Profile = -> Sketch014
  ReferenceAxis = -> Sketch014 [N_Axis]
  Refine = true
  SideType = 0
  Suppressed = false
  Type = 0
  Type2 = 0
FEATURE [Sketcher::SketchObject] Sketch015
  ArcFitTolerance = 1e-06
  AttachmentSupport = -> [Pocket009]
  ExternalGeometry = -> [Pocket009]
  ExternalTypes = [0,0]
  FullyConstrained = true
  MakeInternals = false
  MapMode = 5
  Placement = pos=(0,0,10) rot=(0,0,1;0rad)
  sketch-geometry (7):
    g0: Circle [constr] CenterX=0 CenterY=0 CenterZ=0 NormalX=0 NormalY=0 NormalZ=1 AngleXU=0 Radius=32.5
    g1: ArcOfCircle CenterX=0 CenterY=0 CenterZ=0 NormalX=0 NormalY=0 NormalZ=1 AngleXU=0 Radius=32.5 StartAngle=0.532504 EndAngle=2.60909
    g2: LineSegment StartX=-28 StartY=16.5 StartZ=0 EndX=-31 EndY=16.5 EndZ=0
    g3: LineSegment StartX=31 StartY=16.5 StartZ=0 EndX=28 EndY=16.5 EndZ=0
    g4: LineSegment StartX=-31 StartY=16.5 StartZ=0 EndX=-31 EndY=55 EndZ=0
    g5: LineSegment StartX=-31 StartY=55 StartZ=0 EndX=31 EndY=55 EndZ=0
    g6: LineSegment StartX=31 StartY=55 StartZ=0 EndX=31 EndY=16.5 EndZ=0
  constraints (20):
    c: Coincident(g0,g-1)
    c: Diameter(g0) = 65
    c: Coincident(g1,g0)
    c: PointOnObject(g1,g0)
    c: Coincident(g2,g1)
    c: Horizontal(g2)
    c: Coincident(g3,g1)
    c: Horizontal(g3)
    c: Equal(g3,g2)
    c: Symmetric(g1,g1,g-2)
    c: Distance(g2,g2) = 3
    c: Coincident(g4,g2)
    c: Vertical(g4)
    c: Coincident(g5,g4)
    c: Horizontal(g5)
    c: Coincident(g6,g5)
    c: Coincident(g6,g3)
    c: Vertical(g6)
    c: DistanceY(g5,g-3) = 4
    c: Distance(g-3,g6) = 4
FEATURE [PartDesign::Pocket] Pocket010
  BaseFeature = -> Pocket009
  Direction = (0,0,-1)
  Length = 7
  Length2 = 5
  Profile = -> Sketch015
  ReferenceAxis = -> Sketch015 [N_Axis]
  Refine = true
  SideType = 0
  Suppressed = false
  Type = 0
  Type2 = 0
FEATURE [PartDesign::Mirrored] Mirrored002
  BaseFeature = -> Pocket010
  MirrorPlane = -> XZ_Plane001
  Originals = -> [Pocket010]
  Refine = true
  Suppressed = false
  TransformMode = 0
FEATURE [PartDesign::Chamfer] Chamfer005
  Angle = 45
  Base = -> Mirrored002 [Edge34,Edge56,Edge8,Edge6]
  BaseFeature = -> Mirrored002
  ChamferType = 0
  FlipDirection = false
  Refine = true
  Size = 3
  Size2 = 1
  SupportTransform = false
  Suppressed = false
  UseAllEdges = false
FEATURE [PartDesign::Fillet] Fillet006
  Base = -> Chamfer005 [Edge79,Edge81,Edge91,Edge95]
  BaseFeature = -> Chamfer005
  Radius = 6
  Refine = true
  SupportTransform = false
  Suppressed = false
  UseAllEdges = false
FEATURE [PartDesign::Fillet] Fillet007
  Base = -> Fillet006 [Edge91,Edge95,Edge87,Edge83,Edge41,Edge37,Edge33,Edge29]
  BaseFeature = -> Fillet006
  Radius = 1
  Refine = true
  SupportTransform = false
  Suppressed = false
  UseAllEdges = false
FEATURE [PartDesign::Chamfer] Chamfer006
  Angle = 45
  Base = -> Fillet007 [Face37,Face51]
  BaseFeature = -> Fillet007
  ChamferType = 0
  FlipDirection = false
  Refine = true
  Size = 1
  Size2 = 1
  SupportTransform = false
  Suppressed = false
  UseAllEdges = false
FEATURE [PartDesign::Chamfer] Chamfer007
  Angle = 45
  Base = -> Chamfer006 [Edge91,Edge78,Edge75,Edge88,Edge101,Edge103,Edge86,Edge94]
  BaseFeature = -> Chamfer006
  ChamferType = 0
  FlipDirection = false
  Refine = true
  Size = 1
  Size2 = 1
  SupportTransform = false
  Suppressed = false
  UseAllEdges = false
FEATURE [Sketcher::SketchObject] Sketch016
  ArcFitTolerance = 1e-06
  AttachmentSupport = -> [Chamfer007]
  ExternalGeometry = -> [Chamfer007]
  ExternalTypes = [0,0]
  FullyConstrained = true
  MakeInternals = false
  MapMode = 5
  Placement = pos=(0,0,7) rot=(1,0,0;3.14159rad)
  sketch-geometry (8):
    g0: ArcOfCircle CenterX=14.5 CenterY=66 CenterZ=0 NormalX=0 NormalY=0 NormalZ=1 AngleXU=0 Radius=1.7 StartAngle=-3.6e-15 EndAngle=3.14159
    g1: ArcOfCircle CenterX=14.5 CenterY=63 CenterZ=0 NormalX=0 NormalY=0 NormalZ=1 AngleXU=0 Radius=1.7 StartAngle=3.14159 EndAngle=6.28319
    g2: LineSegment StartX=16.2 StartY=66 StartZ=0 EndX=16.2 EndY=63 EndZ=0
    g3: LineSegment StartX=12.8 StartY=66 StartZ=0 EndX=12.8 EndY=63 EndZ=0
    g4: ArcOfCircle CenterX=-14.5 CenterY=66 CenterZ=0 NormalX=0 NormalY=0 NormalZ=1 AngleXU=0 Radius=1.7 StartAngle=1.1e-15 EndAngle=3.14159
    g5: ArcOfCircle CenterX=-14.5 CenterY=63 CenterZ=0 NormalX=0 NormalY=0 NormalZ=1 AngleXU=0 Radius=1.7 StartAngle=3.14159 EndAngle=6.28319
    g6: LineSegment StartX=-12.8 StartY=66 StartZ=0 EndX=-12.8 EndY=63 EndZ=0
    g7: LineSegment StartX=-16.2 StartY=66 StartZ=0 EndX=-16.2 EndY=63 EndZ=0
  constraints (19):
    c: Tangent(g0,g2) = 1.5708
    c: Tangent(g0,g3) = -1.5708
    c: Tangent(g1,g2) = 1.5708
    c: Tangent(g1,g3) = -1.5708
    c: Equal(g0,g1)
    c: Vertical(g2)
    c: Distance(g0,g-3) = 3
    c: Distance(g1,g-3) = 6
    c: Radius(g0) = 1.7
    c: Distance(g0,g-4) = 4.5
    c: Tangent(g4,g6) = 1.5708
    c: Tangent(g4,g7) = -1.5708
    c: Tangent(g5,g6) = 1.5708
    c: Tangent(g5,g7) = -1.5708
    c: Equal(g4,g5)
    c: Vertical(g6)
    c: Equal(g4,g0)
    c: Equal(g6,g3)
    c: Symmetric(g4,g0,g-2)
FEATURE [PartDesign::Pocket] Pocket011
  BaseFeature = -> Chamfer007
  Direction = (0,0,1)
  Length = 5
  Length2 = 5
  Profile = -> Sketch016
  ReferenceAxis = -> Sketch016 [N_Axis]
  Refine = true
  SideType = 0
  Suppressed = false
  Type = 0
  Type2 = 0
FEATURE [PartDesign::Mirrored] Mirrored003
  BaseFeature = -> Pocket011
  MirrorPlane = -> XZ_Plane001
  Originals = -> [Pocket011]
  Refine = true
  Suppressed = false
  TransformMode = 0
FEATURE [PartDesign::Chamfer] Chamfer008
  Angle = 45
  Base = -> Mirrored003 [Edge100,Edge82]
  BaseFeature = -> Mirrored003
  ChamferType = 0
  FlipDirection = false
  Refine = true
  Size = 1
  Size2 = 1
  SupportTransform = false
  Suppressed = false
  UseAllEdges = false
FEATURE [PartDesign::Chamfer] Chamfer009
  Angle = 45
  Base = -> Chamfer008 [Face65]
  BaseFeature = -> Chamfer008
  ChamferType = 0
  FlipDirection = false
  Refine = true
  Size = 0.6
  Size2 = 1
  SupportTransform = false
  Suppressed = false
  UseAllEdges = false
FEATURE [PartDesign::Chamfer] Chamfer010
  Angle = 45
  Base = -> Chamfer009 [Edge69,Edge74,Edge64]
  BaseFeature = -> Chamfer009
  ChamferType = 0
  FlipDirection = false
  Refine = true
  Size = 0.4
  Size2 = 1
  SupportTransform = false
  Suppressed = false
  UseAllEdges = false
FEATURE [PartDesign::Body] Body001  label="battery-plate"
  AllowCompound = true
  Group = -> [Binder,Sketch013,Pad005,Sketch014,Pocket009,Sketch015,Pocket010,Mirrored002,Chamfer005,Fillet006,Fillet007,Chamfer006,Chamfer007,Sketch016,Pocket011,Mirrored003,Chamfer008,Chamfer009,Chamfer010]
  Origin = -> Origin002
  Placement = pos=(-7.1e-15,0,-20) rot=(0,0,1;0rad)
  Tip = -> Chamfer010
FEATURE [App::Part] Part  label="battery-asm"
  Group = -> [Body,Body001]
  Origin = -> Origin004
FEATURE [App::Point] Origin005  label="Origine003"
  Role = Origin
